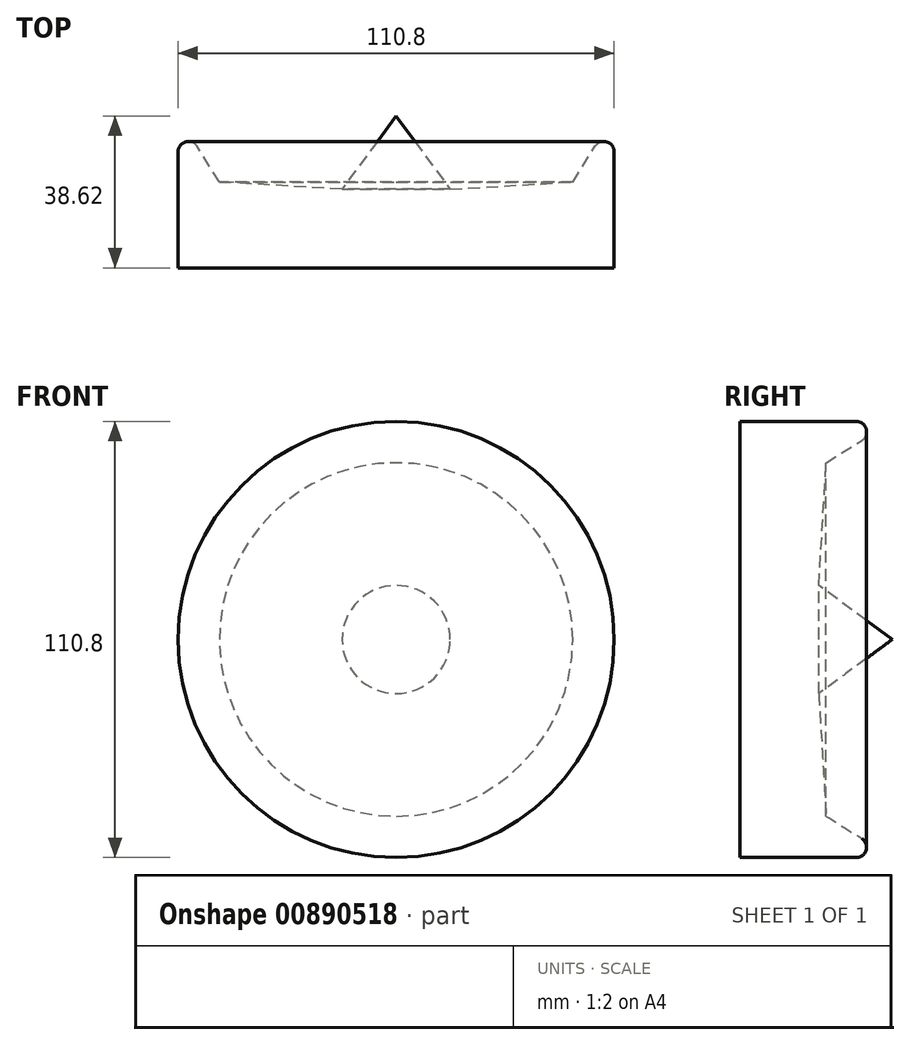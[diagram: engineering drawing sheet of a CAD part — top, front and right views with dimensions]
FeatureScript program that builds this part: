
annotation { "Feature Type Name" : "Feature", "Feature Type Description" : "" }
export const myFeature = defineFeature(function(context is Context, id is Id, definition is map)
    precondition{}
    {
        {
            var Q0;
            Q0=qCreatedBy(makeId("Top.planeOp"),FACE);
            var sketch = newSketch(context, id + "F0", { "sketchPlane" : qUnion([Q0])});
            skLineSegment(sketch, "E0", {"start": v(0, 0) * mm, "end": v(0, 38.62) * mm});
            skLineSegment(sketch, "E1", {"start": v(0, 38.62) * mm, "end": v(-13.73, 20) * mm});
            skLineSegment(sketch, "E2", {"start": v(-13.73, 20) * mm, "end": v(-44.9, 21.85) * mm});
            skLineSegment(sketch, "E3", {"start": v(-44.9, 21.85) * mm, "end": v(-55.4, 38.62) * mm});
            skLineSegment(sketch, "E4", {"start": v(-55.4, 38.62) * mm, "end": v(-55.4, 0) * mm});
            skLineSegment(sketch, "E5", {"start": v(-55.4, 0) * mm, "end": v(0, 0) * mm});
            skLineSegment(sketch, "E6", {"start": v(-13.73, 20) * mm, "end": v(-16.7, 20.18) * mm});
            skSolve(sketch);
        }
        {
            var Q0;
            Q0=makeQuery(id+"F0.imprint","IMPRINT",FACE,{"disambiguationData":[TD([[makeQuery(id+"F0.imprint","IMPRINT",EDGE,{"derivedFrom":sQuery(id+"F0.wireOp",EDGE,"E0")}),1.0]])]});
            var Q1;
            Q1=sQuery(id+"F0.wireOp",EDGE,"E0");
            revolve(context, id + "F1", {"surfaceOperationType" : NewSurfaceOperationType.NEW, "entities" : qUnion([Q0]), "axis" : qUnion([Q1]), "revolveType" : RevolveType.FULL});
        }
        {
            var Q0;
            Q0=makeQuery(id+"F1.opRevolve","SWEPT_EDGE",EDGE,{"disambiguationData":[OSD([sQuery(id+"F0.wireOp",EDGE,"E3"),sQuery(id+"F0.wireOp",EDGE,"E4")])]});
            fillet(context, id + "F2", {"entities" : qUnion([Q0]), "radius" : 2.62 * mm, "tangentPropagation" : true, "allowEdgeOverflow" : false});
        }
    });
